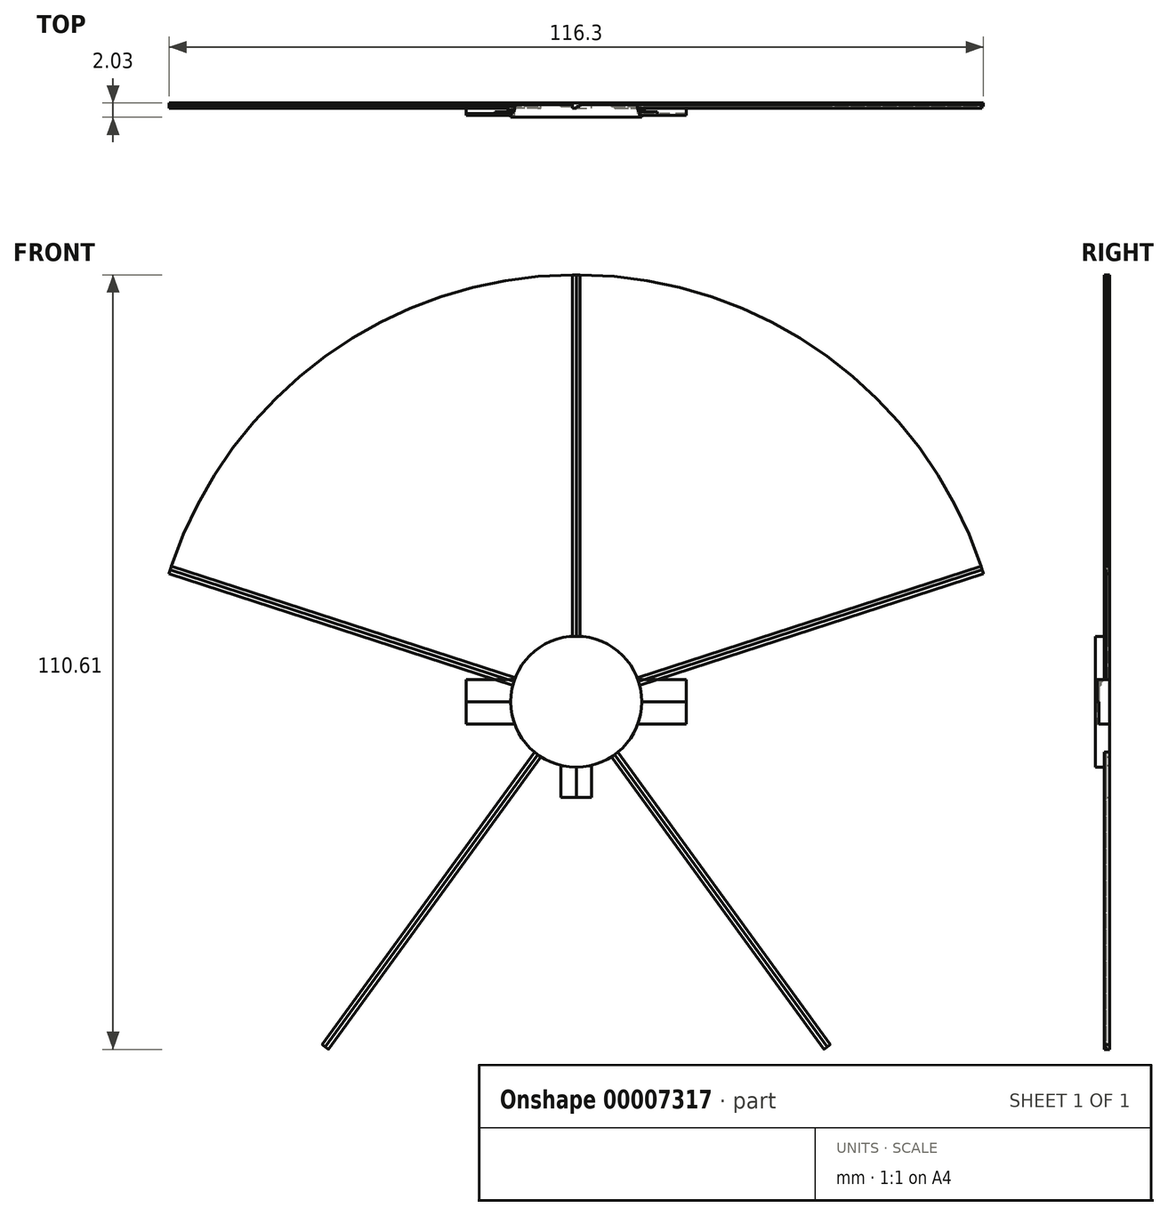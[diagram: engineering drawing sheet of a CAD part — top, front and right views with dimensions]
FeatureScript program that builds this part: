
annotation { "Feature Type Name" : "Feature", "Feature Type Description" : "" }
export const myFeature = defineFeature(function(context is Context, id is Id, definition is map)
    precondition{}
    {
        {
            var Q0;
            Q0=qCreatedBy(makeId("Front.planeOp"),FACE);
            var sketch = newSketch(context, id + "F0", { "sketchPlane" : qUnion([Q0])});
            skCircle(sketch, "E0", {"center": v(0, 0) * mm, "radius": 60.96 * mm});
            skCircle(sketch, "E1", {"center": v(0, 0) * mm, "radius": 9.35 * mm});
            skLineSegment(sketch, "E2", {"start": v(0, 0) * mm, "end": v(0, 60.96) * mm});
            skLineSegment(sketch, "E3", {"start": v(0.57, 9.33) * mm, "end": v(0.57, 60.96) * mm});
            skLineSegment(sketch, "E4.MirrorCS", {"start": v(-0.57, 9.33) * mm, "end": v(-0.57, 60.96) * mm});
            skLineSegment(sketch, "E5", {"start": v(0, 0) * mm, "end": v(0, -9.35) * mm});
            skLineSegment(sketch, "E6", {"start": v(0, -9.35) * mm, "end": v(0, -60.96) * mm});
            skCircle(sketch, "E7", {"center": v(0, -11.52) * mm, "radius": 2.17 * mm});
            skLineSegment(sketch, "E8", {"start": v(-2.17, -13.7) * mm, "end": v(0, -13.7) * mm});
            skLineSegment(sketch, "E9", {"start": v(0, -13.7) * mm, "end": v(2.17, -13.7) * mm});
            skLineSegment(sketch, "E10", {"start": v(2.17, -13.7) * mm, "end": v(2.17, -9.1) * mm});
            skLineSegment(sketch, "E11", {"start": v(-2.17, -9.1) * mm, "end": v(-2.17, -13.7) * mm});
            skLineSegment(sketch, "E12", {"start": v(-8.8, 3.17) * mm, "end": v(-15.7, 3.17) * mm});
            skLineSegment(sketch, "E13", {"start": v(-15.7, 3.17) * mm, "end": v(-15.7, 0) * mm});
            skLineSegment(sketch, "E14", {"start": v(-15.7, 0) * mm, "end": v(-15.7, -3.18) * mm});
            skLineSegment(sketch, "E15", {"start": v(-15.7, -3.18) * mm, "end": v(-8.8, -3.18) * mm});
            skLineSegment(sketch, "E16", {"start": v(-15.7, 0) * mm, "end": v(0, 0) * mm});
            skLineSegment(sketch, "E17.MirrorCS", {"start": v(8.8, 3.17) * mm, "end": v(15.7, 3.17) * mm});
            skLineSegment(sketch, "E18.MirrorCS", {"start": v(15.7, 0) * mm, "end": v(0, 0) * mm});
            skLineSegment(sketch, "E19.MirrorCS", {"start": v(15.7, 3.17) * mm, "end": v(15.7, 0) * mm});
            skLineSegment(sketch, "E20.MirrorCS", {"start": v(15.7, 0) * mm, "end": v(15.7, -3.18) * mm});
            skLineSegment(sketch, "E21.MirrorCS", {"start": v(15.7, -3.18) * mm, "end": v(8.8, -3.18) * mm});
            skLineSegment(sketch, "E22.1.0", {"start": v(-8.7, 3.42) * mm, "end": v(-57.8, 19.37) * mm});
            skLineSegment(sketch, "E22.1.1", {"start": v(0, 0) * mm, "end": v(-57.98, 18.84) * mm});
            skLineSegment(sketch, "E22.1.2", {"start": v(-9.05, 2.35) * mm, "end": v(-58.15, 18.3) * mm});
            skLineSegment(sketch, "E22.2.0", {"start": v(-5.94, -7.22) * mm, "end": v(-36.29, -48.98) * mm});
            skLineSegment(sketch, "E22.2.1", {"start": v(0, 0) * mm, "end": v(-35.83, -49.32) * mm});
            skLineSegment(sketch, "E22.2.2", {"start": v(-5.03, -7.88) * mm, "end": v(-35.37, -49.65) * mm});
            skLineSegment(sketch, "E22.3.0", {"start": v(5.03, -7.88) * mm, "end": v(35.37, -49.65) * mm});
            skLineSegment(sketch, "E22.3.1", {"start": v(0, 0) * mm, "end": v(35.83, -49.32) * mm});
            skLineSegment(sketch, "E22.3.2", {"start": v(5.94, -7.22) * mm, "end": v(36.29, -48.98) * mm});
            skLineSegment(sketch, "E22.4.0", {"start": v(9.05, 2.35) * mm, "end": v(58.15, 18.3) * mm});
            skLineSegment(sketch, "E22.4.1", {"start": v(0, 0) * mm, "end": v(57.98, 18.84) * mm});
            skLineSegment(sketch, "E22.4.2", {"start": v(8.7, 3.42) * mm, "end": v(57.8, 19.37) * mm});
            skSolve(sketch);
        }
        {
            var Q0;
            {var subQ0=sQuery(id+"F0.wireOp",EDGE,"E3");Q0=makeQuery(id+"F0.imprint","IMPRINT",FACE,{"disambiguationData":[TD([[makeQuery(id+"F0.imprint","IMPRINT",EDGE,{"derivedFrom":subQ0}),-1.0]])]});}
            var Q1;
            {var subQ0=sQuery(id+"F0.wireOp",EDGE,"E19.MirrorCS");Q1=makeQuery(id+"F0.imprint","IMPRINT",FACE,{"disambiguationData":[TD([[makeQuery(id+"F0.imprint","IMPRINT",EDGE,{"derivedFrom":subQ0}),1.0]])]});}
            var Q2;
            {var subQ3=sQuery(id+"F0.wireOp",EDGE,"E9");Q2=makeQuery(id+"F0.imprint","IMPRINT",FACE,{"disambiguationData":[TD([[makeQuery(id+"F0.imprint","IMPRINT",EDGE,{"derivedFrom":subQ3}),-1.0]])]});}
            var Q3;
            {var subQ4=sQuery(id+"F0.wireOp",EDGE,"E8");Q3=makeQuery(id+"F0.imprint","IMPRINT",FACE,{"disambiguationData":[TD([[makeQuery(id+"F0.imprint","IMPRINT",EDGE,{"derivedFrom":subQ4}),-1.0]])]});}
            var Q4;
            {var subQ0=sQuery(id+"F0.wireOp",EDGE,"E13");Q4=makeQuery(id+"F0.imprint","IMPRINT",FACE,{"disambiguationData":[TD([[makeQuery(id+"F0.imprint","IMPRINT",EDGE,{"derivedFrom":subQ0}),-1.0]])]});}
            var Q5;
            {var subQ0=sQuery(id+"F0.wireOp",EDGE,"E4.MirrorCS");Q5=makeQuery(id+"F0.imprint","IMPRINT",FACE,{"disambiguationData":[TD([[makeQuery(id+"F0.imprint","IMPRINT",EDGE,{"derivedFrom":subQ0}),1.0]])]});}
            extrude(context, id + "F1", {"entities" : qUnion([Q0, Q1, Q2, Q3, Q4, Q5]), "depth" : 0.25 * mm});
        }
        {
            var Q0;
            {var subQ0=sQuery(id+"F0.wireOp",EDGE,"E22.2.0");Q0=makeQuery(id+"F0.imprint","IMPRINT",FACE,{"disambiguationData":[TD([[makeQuery(id+"F0.imprint","IMPRINT",EDGE,{"derivedFrom":subQ0}),1.0]])]});}
            var Q1;
            {var subQ0=sQuery(id+"F0.wireOp",EDGE,"E22.1.0");Q1=makeQuery(id+"F0.imprint","IMPRINT",FACE,{"disambiguationData":[TD([[makeQuery(id+"F0.imprint","IMPRINT",EDGE,{"derivedFrom":subQ0}),1.0]])]});}
            var Q2;
            {var subQ0=sQuery(id+"F0.wireOp",EDGE,"E12");var subQ1=sQuery(id+"F0.wireOp",EDGE,"E1");var subQ2=makeQuery(id+"F0.imprint","INTERSECT",VERTEX,{"derivedFrom":[subQ1,subQ0]});Q2=makeQuery(id+"F0.imprint","IMPRINT",FACE,{"disambiguationData":[TD([[makeQuery(id+"F0.imprint","IMPRINT",EDGE,{"disambiguationData":[TD([[subQ2,-1.0]])],"derivedFrom":subQ1}),-1.0]])]});}
            var Q3;
            {var subQ3=sQuery(id+"F0.wireOp",EDGE,"E3");Q3=makeQuery(id+"F0.imprint","IMPRINT",FACE,{"disambiguationData":[TD([[makeQuery(id+"F0.imprint","IMPRINT",EDGE,{"derivedFrom":subQ3}),1.0]])]});}
            var Q4;
            {var subQ0=sQuery(id+"F0.wireOp",EDGE,"E22.4.0");var subQ1=sQuery(id+"F0.wireOp",EDGE,"E0");var subQ2=makeQuery(id+"F0.imprint","INTERSECT",VERTEX,{"derivedFrom":[subQ1,subQ0]});Q4=makeQuery(id+"F0.imprint","IMPRINT",FACE,{"disambiguationData":[TD([[makeQuery(id+"F0.imprint","IMPRINT",EDGE,{"disambiguationData":[TD([[subQ2,-1.0]])],"derivedFrom":subQ1}),1.0]])]});}
            var Q5;
            {var subQ0=sQuery(id+"F0.wireOp",EDGE,"E22.4.0");var subQ1=sQuery(id+"F0.wireOp",EDGE,"E1");var subQ2=makeQuery(id+"F0.imprint","INTERSECT",VERTEX,{"derivedFrom":[subQ1,subQ0]});Q5=makeQuery(id+"F0.imprint","IMPRINT",FACE,{"disambiguationData":[TD([[makeQuery(id+"F0.imprint","IMPRINT",EDGE,{"disambiguationData":[TD([[subQ2,-1.0]])],"derivedFrom":subQ1}),-1.0]])]});}
            var Q6;
            {var subQ0=sQuery(id+"F0.wireOp",EDGE,"E22.3.0");Q6=makeQuery(id+"F0.imprint","IMPRINT",FACE,{"disambiguationData":[TD([[makeQuery(id+"F0.imprint","IMPRINT",EDGE,{"derivedFrom":subQ0}),1.0]])]});}
            var Q7;
            {var subQ1=sQuery(id+"F0.wireOp",EDGE,"E1");var subQ3=sQuery(id+"F0.wireOp",EDGE,"E11");var subQ4=makeQuery(id+"F0.imprint","INTERSECT",VERTEX,{"derivedFrom":[subQ1,subQ3]});Q7=makeQuery(id+"F0.imprint","IMPRINT",FACE,{"disambiguationData":[TD([[makeQuery(id+"F0.imprint","IMPRINT",EDGE,{"disambiguationData":[TD([[subQ4,-1.0]])],"derivedFrom":subQ3}),1.0]])]});}
            var Q8;
            {var subQ0=sQuery(id+"F0.wireOp",EDGE,"E7");var subQ4=makeQuery(id+"F0.imprint","INTERSECT",VERTEX,{"derivedFrom":[subQ0,sQuery(id+"F0.wireOp",EDGE,"E11")]});Q8=makeQuery(id+"F0.imprint","IMPRINT",FACE,{"disambiguationData":[TD([[makeQuery(id+"F0.imprint","IMPRINT",EDGE,{"disambiguationData":[TD([[subQ4,1.0]])],"derivedFrom":subQ0}),1.0]])]});}
            var Q9;
            {var subQ0=sQuery(id+"F0.wireOp",EDGE,"E8");Q9=makeQuery(id+"F0.imprint","IMPRINT",FACE,{"disambiguationData":[TD([[makeQuery(id+"F0.imprint","IMPRINT",EDGE,{"derivedFrom":subQ0}),1.0]])]});}
            extrude(context, id + "F2", {"entities" : qUnion([Q0, Q1, Q2, Q3, Q4, Q5, Q6, Q7, Q8, Q9]), "operationType" : NewBodyOperationType.ADD, "depth" : 0.5 * mm});
        }
        {
            var Q0;
            {var subQ1=sQuery(id+"F0.wireOp",EDGE,"E1");var subQ3=sQuery(id+"F0.wireOp",EDGE,"E10");var subQ4=makeQuery(id+"F0.imprint","INTERSECT",VERTEX,{"derivedFrom":[subQ1,subQ3]});Q0=makeQuery(id+"F0.imprint","IMPRINT",FACE,{"disambiguationData":[TD([[makeQuery(id+"F0.imprint","IMPRINT",EDGE,{"disambiguationData":[TD([[subQ4,1.0]])],"derivedFrom":subQ3}),1.0]])]});}
            var Q1;
            {var subQ0=sQuery(id+"F0.wireOp",EDGE,"E9");Q1=makeQuery(id+"F0.imprint","IMPRINT",FACE,{"disambiguationData":[TD([[makeQuery(id+"F0.imprint","IMPRINT",EDGE,{"derivedFrom":subQ0}),1.0]])]});}
            var Q2;
            {var subQ0=sQuery(id+"F0.wireOp",EDGE,"E7");var subQ4=makeQuery(id+"F0.imprint","INTERSECT",VERTEX,{"derivedFrom":[subQ0,sQuery(id+"F0.wireOp",EDGE,"E10")]});Q2=makeQuery(id+"F0.imprint","IMPRINT",FACE,{"disambiguationData":[TD([[makeQuery(id+"F0.imprint","IMPRINT",EDGE,{"disambiguationData":[TD([[subQ4,-1.0]])],"derivedFrom":subQ0}),1.0]])]});}
            var Q3;
            {var subQ3=sQuery(id+"F0.wireOp",EDGE,"E22.2.2");Q3=makeQuery(id+"F0.imprint","IMPRINT",FACE,{"disambiguationData":[TD([[makeQuery(id+"F0.imprint","IMPRINT",EDGE,{"derivedFrom":subQ3}),-1.0]])]});}
            var Q4;
            {var subQ0=sQuery(id+"F0.wireOp",EDGE,"E22.1.1");var subQ1=sQuery(id+"F0.wireOp",EDGE,"E0");var subQ2=makeQuery(id+"F0.imprint","INTERSECT",VERTEX,{"derivedFrom":[subQ1,subQ0]});Q4=makeQuery(id+"F0.imprint","IMPRINT",FACE,{"disambiguationData":[TD([[makeQuery(id+"F0.imprint","IMPRINT",EDGE,{"disambiguationData":[TD([[subQ2,-1.0]])],"derivedFrom":subQ1}),1.0]])]});}
            var Q5;
            {var subQ0=sQuery(id+"F0.wireOp",EDGE,"E22.1.2");var subQ1=sQuery(id+"F0.wireOp",EDGE,"E1");var subQ2=makeQuery(id+"F0.imprint","INTERSECT",VERTEX,{"derivedFrom":[subQ1,subQ0]});Q5=makeQuery(id+"F0.imprint","IMPRINT",FACE,{"disambiguationData":[TD([[makeQuery(id+"F0.imprint","IMPRINT",EDGE,{"disambiguationData":[TD([[subQ2,1.0]])],"derivedFrom":subQ1}),-1.0]])]});}
            var Q6;
            {var subQ3=sQuery(id+"F0.wireOp",EDGE,"E4.MirrorCS");Q6=makeQuery(id+"F0.imprint","IMPRINT",FACE,{"disambiguationData":[TD([[makeQuery(id+"F0.imprint","IMPRINT",EDGE,{"derivedFrom":subQ3}),-1.0]])]});}
            var Q7;
            {var subQ5=sQuery(id+"F0.wireOp",EDGE,"E22.4.2");Q7=makeQuery(id+"F0.imprint","IMPRINT",FACE,{"disambiguationData":[TD([[makeQuery(id+"F0.imprint","IMPRINT",EDGE,{"derivedFrom":subQ5}),-1.0]])]});}
            var Q8;
            {var subQ0=sQuery(id+"F0.wireOp",EDGE,"E17.MirrorCS");var subQ1=sQuery(id+"F0.wireOp",EDGE,"E1");var subQ2=makeQuery(id+"F0.imprint","INTERSECT",VERTEX,{"derivedFrom":[subQ1,subQ0]});Q8=makeQuery(id+"F0.imprint","IMPRINT",FACE,{"disambiguationData":[TD([[makeQuery(id+"F0.imprint","IMPRINT",EDGE,{"disambiguationData":[TD([[subQ2,1.0]])],"derivedFrom":subQ1}),-1.0]])]});}
            var Q9;
            {var subQ3=sQuery(id+"F0.wireOp",EDGE,"E22.3.2");Q9=makeQuery(id+"F0.imprint","IMPRINT",FACE,{"disambiguationData":[TD([[makeQuery(id+"F0.imprint","IMPRINT",EDGE,{"derivedFrom":subQ3}),-1.0]])]});}
            extrude(context, id + "F3", {"entities" : qUnion([Q0, Q1, Q2, Q3, Q4, Q5, Q6, Q7, Q8, Q9]), "operationType" : NewBodyOperationType.ADD, "depth" : 0.76 * mm});
        }
        {
            var Q0;
            {var subQ0=sQuery(id+"F0.wireOp",EDGE,"E12");var subQ1=sQuery(id+"F0.wireOp",EDGE,"E1");var subQ2=makeQuery(id+"F0.imprint","INTERSECT",VERTEX,{"derivedFrom":[subQ1,subQ0]});Q0=makeQuery(id+"F0.imprint","IMPRINT",FACE,{"disambiguationData":[TD([[makeQuery(id+"F0.imprint","IMPRINT",EDGE,{"disambiguationData":[TD([[subQ2,-1.0]])],"derivedFrom":subQ1}),-1.0]])]});}
            var Q1;
            {var subQ0=sQuery(id+"F0.wireOp",EDGE,"E17.MirrorCS");var subQ1=sQuery(id+"F0.wireOp",EDGE,"E1");var subQ2=makeQuery(id+"F0.imprint","INTERSECT",VERTEX,{"derivedFrom":[subQ1,subQ0]});Q1=makeQuery(id+"F0.imprint","IMPRINT",FACE,{"disambiguationData":[TD([[makeQuery(id+"F0.imprint","IMPRINT",EDGE,{"disambiguationData":[TD([[subQ2,1.0]])],"derivedFrom":subQ1}),-1.0]])]});}
            extrude(context, id + "F4", {"entities" : qUnion([Q0, Q1]), "operationType" : NewBodyOperationType.ADD, "depth" : 1.02 * mm});
        }
        {
            var Q0;
            {var subQ0=sQuery(id+"F0.wireOp",EDGE,"E22.1.2");var subQ1=sQuery(id+"F0.wireOp",EDGE,"E1");var subQ2=makeQuery(id+"F0.imprint","INTERSECT",VERTEX,{"derivedFrom":[subQ1,subQ0]});Q0=makeQuery(id+"F0.imprint","IMPRINT",FACE,{"disambiguationData":[TD([[makeQuery(id+"F0.imprint","IMPRINT",EDGE,{"disambiguationData":[TD([[subQ2,1.0]])],"derivedFrom":subQ1}),-1.0]])]});}
            var Q1;
            {var subQ0=sQuery(id+"F0.wireOp",EDGE,"E22.4.0");var subQ1=sQuery(id+"F0.wireOp",EDGE,"E1");var subQ2=makeQuery(id+"F0.imprint","INTERSECT",VERTEX,{"derivedFrom":[subQ1,subQ0]});Q1=makeQuery(id+"F0.imprint","IMPRINT",FACE,{"disambiguationData":[TD([[makeQuery(id+"F0.imprint","IMPRINT",EDGE,{"disambiguationData":[TD([[subQ2,-1.0]])],"derivedFrom":subQ1}),-1.0]])]});}
            extrude(context, id + "F5", {"entities" : qUnion([Q0, Q1]), "operationType" : NewBodyOperationType.ADD, "depth" : 1.27 * mm});
        }
        {
            var Q0;
            {var subQ1=sQuery(id+"F0.wireOp",EDGE,"E13");Q0=makeQuery(id+"F0.imprint","IMPRINT",FACE,{"disambiguationData":[TD([[makeQuery(id+"F0.imprint","IMPRINT",EDGE,{"derivedFrom":subQ1}),1.0]])]});}
            var Q1;
            {var subQ4=sQuery(id+"F0.wireOp",EDGE,"E20.MirrorCS");Q1=makeQuery(id+"F0.imprint","IMPRINT",FACE,{"disambiguationData":[TD([[makeQuery(id+"F0.imprint","IMPRINT",EDGE,{"derivedFrom":subQ4}),-1.0]])]});}
            extrude(context, id + "F6", {"entities" : qUnion([Q0, Q1]), "operationType" : NewBodyOperationType.ADD, "depth" : 1.52 * mm});
        }
        {
            var Q0;
            {var subQ4=sQuery(id+"F0.wireOp",EDGE,"E14");Q0=makeQuery(id+"F0.imprint","IMPRINT",FACE,{"disambiguationData":[TD([[makeQuery(id+"F0.imprint","IMPRINT",EDGE,{"derivedFrom":subQ4}),1.0]])]});}
            var Q1;
            {var subQ0=sQuery(id+"F0.wireOp",EDGE,"E19.MirrorCS");Q1=makeQuery(id+"F0.imprint","IMPRINT",FACE,{"disambiguationData":[TD([[makeQuery(id+"F0.imprint","IMPRINT",EDGE,{"derivedFrom":subQ0}),-1.0]])]});}
            extrude(context, id + "F7", {"entities" : qUnion([Q0, Q1]), "operationType" : NewBodyOperationType.ADD, "depth" : 1.78 * mm});
        }
        {
            var Q0;
            {var subQ0=sQuery(id+"F0.wireOp",EDGE,"E1");var subQ5=makeQuery(id+"F0.imprint","INTERSECT",VERTEX,{"derivedFrom":[subQ0,sQuery(id+"F0.wireOp",EDGE,"E4.MirrorCS")]});Q0=makeQuery(id+"F0.imprint","IMPRINT",FACE,{"disambiguationData":[TD([[makeQuery(id+"F0.imprint","IMPRINT",EDGE,{"disambiguationData":[TD([[subQ5,1.0]])],"derivedFrom":subQ0}),1.0]])]});}
            var Q1;
            {var subQ0=sQuery(id+"F0.wireOp",EDGE,"E1");var subQ1=makeQuery(id+"F0.imprint","INTERSECT",VERTEX,{"derivedFrom":[subQ0,sQuery(id+"F0.wireOp",EDGE,"E22.1.2")]});Q1=makeQuery(id+"F0.imprint","IMPRINT",FACE,{"disambiguationData":[TD([[makeQuery(id+"F0.imprint","IMPRINT",EDGE,{"disambiguationData":[TD([[subQ1,1.0]])],"derivedFrom":subQ0}),1.0]])]});}
            var Q2;
            {var subQ0=sQuery(id+"F0.wireOp",EDGE,"E1");var subQ7=makeQuery(id+"F0.imprint","INTERSECT",VERTEX,{"derivedFrom":[subQ0,sQuery(id+"F0.wireOp",EDGE,"E15")]});Q2=makeQuery(id+"F0.imprint","IMPRINT",FACE,{"disambiguationData":[TD([[makeQuery(id+"F0.imprint","IMPRINT",EDGE,{"disambiguationData":[TD([[subQ7,1.0]])],"derivedFrom":subQ0}),1.0]])]});}
            var Q3;
            {var subQ0=sQuery(id+"F0.wireOp",EDGE,"E5");Q3=makeQuery(id+"F0.imprint","IMPRINT",FACE,{"disambiguationData":[TD([[makeQuery(id+"F0.imprint","IMPRINT",EDGE,{"derivedFrom":subQ0}),-1.0]])]});}
            var Q4;
            {var subQ5=sQuery(id+"F0.wireOp",EDGE,"E5");Q4=makeQuery(id+"F0.imprint","IMPRINT",FACE,{"disambiguationData":[TD([[makeQuery(id+"F0.imprint","IMPRINT",EDGE,{"derivedFrom":subQ5}),1.0]])]});}
            var Q5;
            {var subQ3=sQuery(id+"F0.wireOp",EDGE,"E1");var subQ6=makeQuery(id+"F0.imprint","INTERSECT",VERTEX,{"derivedFrom":[subQ3,sQuery(id+"F0.wireOp",EDGE,"E22.3.2")]});Q5=makeQuery(id+"F0.imprint","IMPRINT",FACE,{"disambiguationData":[TD([[makeQuery(id+"F0.imprint","IMPRINT",EDGE,{"disambiguationData":[TD([[subQ6,1.0]])],"derivedFrom":subQ3}),1.0]])]});}
            var Q6;
            {var subQ0=sQuery(id+"F0.wireOp",EDGE,"E1");var subQ1=makeQuery(id+"F0.imprint","INTERSECT",VERTEX,{"derivedFrom":[subQ0,sQuery(id+"F0.wireOp",EDGE,"E22.4.0")]});Q6=makeQuery(id+"F0.imprint","IMPRINT",FACE,{"disambiguationData":[TD([[makeQuery(id+"F0.imprint","IMPRINT",EDGE,{"disambiguationData":[TD([[subQ1,1.0]])],"derivedFrom":subQ0}),1.0]])]});}
            var Q7;
            {var subQ0=sQuery(id+"F0.wireOp",EDGE,"E1");var subQ5=makeQuery(id+"F0.imprint","INTERSECT",VERTEX,{"derivedFrom":[subQ0,sQuery(id+"F0.wireOp",EDGE,"E17.MirrorCS")]});Q7=makeQuery(id+"F0.imprint","IMPRINT",FACE,{"disambiguationData":[TD([[makeQuery(id+"F0.imprint","IMPRINT",EDGE,{"disambiguationData":[TD([[subQ5,1.0]])],"derivedFrom":subQ0}),1.0]])]});}
            extrude(context, id + "F8", {"entities" : qUnion([Q0, Q1, Q2, Q3, Q4, Q5, Q6, Q7]), "operationType" : NewBodyOperationType.ADD, "depth" : 2.03 * mm});
        }
    });
